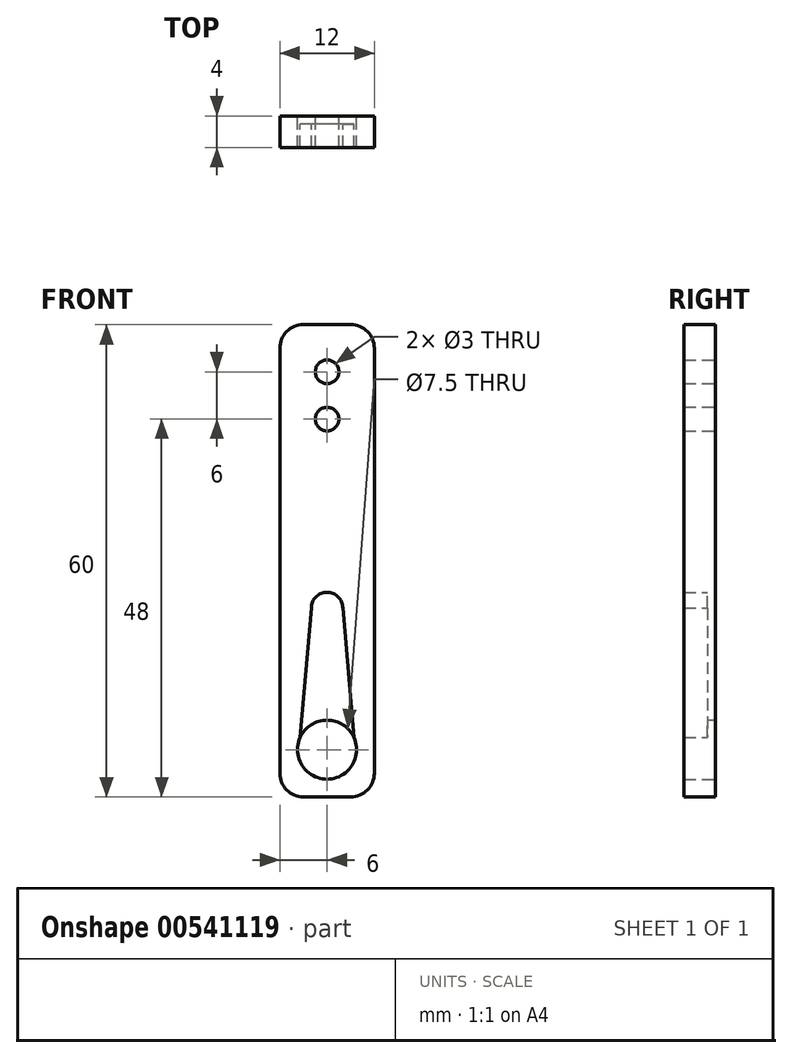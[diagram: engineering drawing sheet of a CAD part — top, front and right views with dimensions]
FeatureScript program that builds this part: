
annotation { "Feature Type Name" : "Feature", "Feature Type Description" : "" }
export const myFeature = defineFeature(function(context is Context, id is Id, definition is map)
    precondition{}
    {
        {
            var Q0;
            Q0=qCreatedBy(makeId("Front.planeOp"),FACE);
            var sketch = newSketch(context, id + "F0", { "sketchPlane" : qUnion([Q0])});
            skLineSegment(sketch, "E0.bottom", {"start": v(3, -30) * mm, "end": v(-3, -30) * mm});
            skLineSegment(sketch, "E0.top", {"start": v(3, 30) * mm, "end": v(-3, 30) * mm});
            skLineSegment(sketch, "E0.left", {"start": v(6, -27) * mm, "end": v(6, 27) * mm});
            skLineSegment(sketch, "E0.right", {"start": v(-6, -27) * mm, "end": v(-6, 27) * mm});
            skPoint(sketch, "E0.middle", {"position": v(0, 0) * mm});
            skLineSegment(sketch, "E1", {"start": v(-6, -30) * mm, "end": v(6, -18) * mm, "construction": true});
            skLineSegment(sketch, "E2", {"start": v(6, -30) * mm, "end": v(-6, -18) * mm, "construction": true});
            skArc(sketch, "E3", {"start": v(-3.42, -22.47) * mm, "mid": v(0, -27.75) * mm, "end": v(3.42, -22.47) * mm});
            skLineSegment(sketch, "E4", {"start": v(0, -24) * mm, "end": v(0, -4) * mm, "construction": true});
            skArc(sketch, "E5", {"start": v(2, -6) * mm, "mid": v(0, -4) * mm, "end": v(-2, -6) * mm});
            skLineSegment(sketch, "E6", {"start": v(-2, -6) * mm, "end": v(-3.42, -22.47) * mm});
            skPoint(sketch, "E7.visualSharp", {"position": v(-6, -30) * mm});
            skArc(sketch, "E7.filletArc", {"start": v(-6, -27) * mm, "mid": v(-5.12, -29.12) * mm, "end": v(-3, -30) * mm});
            skPoint(sketch, "E8.visualSharp", {"position": v(6, -30) * mm});
            skArc(sketch, "E8.filletArc", {"start": v(3, -30) * mm, "mid": v(5.12, -29.12) * mm, "end": v(6, -27) * mm});
            skPoint(sketch, "E9.visualSharp", {"position": v(-6, 30) * mm});
            skArc(sketch, "E9.filletArc", {"start": v(-3, 30) * mm, "mid": v(-5.12, 29.12) * mm, "end": v(-6, 27) * mm});
            skPoint(sketch, "E10.visualSharp", {"position": v(6, 30) * mm});
            skArc(sketch, "E10.filletArc", {"start": v(6, 27) * mm, "mid": v(5.12, 29.12) * mm, "end": v(3, 30) * mm});
            skLineSegment(sketch, "E11", {"start": v(2, -6) * mm, "end": v(3.42, -22.47) * mm});
            skCircle(sketch, "E12", {"center": v(0, -24) * mm, "radius": 3.75 * mm});
            skLineSegment(sketch, "E13", {"start": v(0, 30) * mm, "end": v(0, -4) * mm, "construction": true});
            skCircle(sketch, "E14", {"center": v(0, 24) * mm, "radius": 1.5 * mm});
            skCircle(sketch, "E15", {"center": v(0, 18) * mm, "radius": 1.5 * mm});
            skSolve(sketch);
        }
        {
            var Q0;
            Q0=makeQuery(id+"F0.imprint","IMPRINT",FACE,{"disambiguationData":[TD([[makeQuery(id+"F0.imprint","IMPRINT",EDGE,{"derivedFrom":sQuery(id+"F0.wireOp",EDGE,"E0.bottom")}),-1.0]])]});
            extrude(context, id + "F1", {"entities" : qUnion([Q0]), "depth" : 4 * mm, "offsetDistance" : 25 * mm});
        }
        {
            var Q0;
            Q0=makeQuery(id+"F0.imprint","IMPRINT",FACE,{"disambiguationData":[TD([[makeQuery(id+"F0.imprint","IMPRINT",EDGE,{"derivedFrom":sQuery(id+"F0.wireOp",EDGE,"E5")}),1.0]])]});
            extrude(context, id + "F2", {"entities" : qUnion([Q0]), "operationType" : NewBodyOperationType.ADD, "depth" : 1 * mm, "offsetDistance" : 25 * mm});
        }
    });
